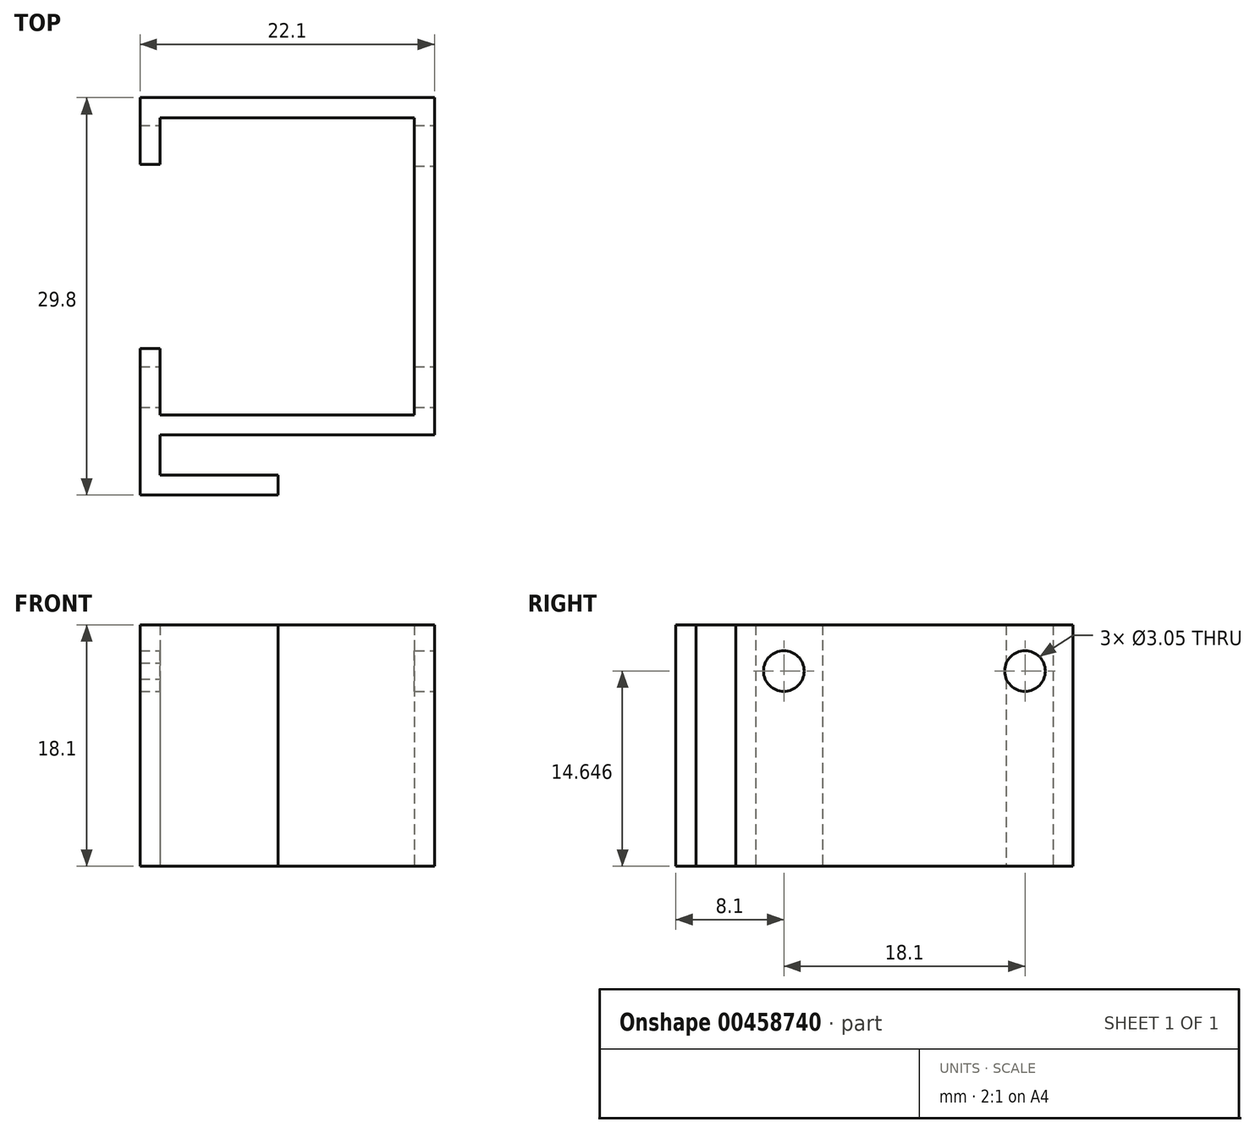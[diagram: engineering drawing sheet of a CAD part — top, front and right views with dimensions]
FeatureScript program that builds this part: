
annotation { "Feature Type Name" : "Feature", "Feature Type Description" : "" }
export const myFeature = defineFeature(function(context is Context, id is Id, definition is map)
    precondition{}
    {
        {
            var Q0;
            Q0=qCreatedBy(makeId("Top.planeOp"),FACE);
            var sketch = newSketch(context, id + "F0", { "sketchPlane" : qUnion([Q0])});
            skLineSegment(sketch, "E0.bottom", {"start": v(-22.1, 18.8) * mm, "end": v(-20.6, 18.8) * mm});
            skLineSegment(sketch, "E0.top", {"start": v(-22.1, 13.8) * mm, "end": v(-20.6, 13.8) * mm});
            skLineSegment(sketch, "E0.left", {"start": v(-22.1, 18.8) * mm, "end": v(-22.1, 13.8) * mm});
            skLineSegment(sketch, "E0.right", {"start": v(-20.6, 18.8) * mm, "end": v(-20.6, 13.8) * mm});
            skPoint(sketch, "E1.oppositeSnap0", {"position": v(-22.1, 17.3) * mm});
            skLineSegment(sketch, "E1.bottom", {"start": v(-22.1, 18.8) * mm, "end": v(0, 18.8) * mm});
            skLineSegment(sketch, "E1.top", {"start": v(-22.1, 17.3) * mm, "end": v(0, 17.3) * mm});
            skLineSegment(sketch, "E1.left", {"start": v(-22.1, 18.8) * mm, "end": v(-22.1, 17.3) * mm});
            skLineSegment(sketch, "E1.right", {"start": v(0, 18.8) * mm, "end": v(0, 17.3) * mm});
            skLineSegment(sketch, "E2.bottom", {"start": v(0, 18.8) * mm, "end": v(-1.5, 18.8) * mm});
            skLineSegment(sketch, "E2.top", {"start": v(0, -6.5) * mm, "end": v(-1.5, -6.5) * mm});
            skLineSegment(sketch, "E2.left", {"start": v(0, 18.8) * mm, "end": v(0, -6.5) * mm});
            skLineSegment(sketch, "E2.right", {"start": v(-1.5, 18.8) * mm, "end": v(-1.5, -6.5) * mm});
            skLineSegment(sketch, "E3.bottom", {"start": v(0, -6.5) * mm, "end": v(-22.1, -6.5) * mm});
            skLineSegment(sketch, "E3.top", {"start": v(0, -5) * mm, "end": v(-22.1, -5) * mm});
            skLineSegment(sketch, "E3.left", {"start": v(0, -6.5) * mm, "end": v(0, -5) * mm});
            skLineSegment(sketch, "E3.right", {"start": v(-22.1, -6.5) * mm, "end": v(-22.1, -5) * mm});
            skLineSegment(sketch, "E4.bottom", {"start": v(-22.1, -6.5) * mm, "end": v(-20.6, -6.5) * mm});
            skLineSegment(sketch, "E4.top", {"start": v(-22.1, 0) * mm, "end": v(-20.6, 0) * mm});
            skLineSegment(sketch, "E4.left", {"start": v(-22.1, -6.5) * mm, "end": v(-22.1, 0) * mm});
            skLineSegment(sketch, "E4.right", {"start": v(-20.6, -6.5) * mm, "end": v(-20.6, 0) * mm});
            skLineSegment(sketch, "E5.top", {"start": v(-22.1, -11) * mm, "end": v(-20.6, -11) * mm});
            skLineSegment(sketch, "E5.left", {"start": v(-22.1, -6.5) * mm, "end": v(-22.1, -11) * mm});
            skLineSegment(sketch, "E5.right", {"start": v(-20.6, -6.5) * mm, "end": v(-20.6, -11) * mm});
            skPoint(sketch, "E6.oppositeSnap0", {"position": v(-20.6, -9.5) * mm});
            skLineSegment(sketch, "E6.bottom", {"start": v(-22.1, -11) * mm, "end": v(-11.74, -11) * mm});
            skLineSegment(sketch, "E6.top", {"start": v(-22.1, -9.5) * mm, "end": v(-11.74, -9.5) * mm});
            skLineSegment(sketch, "E6.left", {"start": v(-22.1, -11) * mm, "end": v(-22.1, -9.5) * mm});
            skLineSegment(sketch, "E6.right", {"start": v(-11.74, -11) * mm, "end": v(-11.74, -9.5) * mm});
            skSolve(sketch);
        }
        {
            var Q0;
            Q0 = qSketchRegion(id + "F0", true);
            extrude(context, id + "F1", {"entities" : qUnion([Q0]), "depth" : 18.1 * mm, "offsetDistance" : 25 * mm});
        }
        {
            var Q0;
            Q0=makeQuery(id+"F1.opExtrude","SWEPT_FACE",FACE,{"disambiguationData":[OSD([sQuery(id+"F0.wireOp",EDGE,"E2.left"),sQuery(id+"F0.wireOp",EDGE,"E3.left")])]});
            var sketch = newSketch(context, id + "F2", { "sketchPlane" : qUnion([Q0])});
            skPoint(sketch, "E7.middle", {"position": v(6.15, 9.05) * mm});
            skLineSegment(sketch, "E8.bottom", {"start": v(17.33, 0) * mm, "end": v(17.32, 18.1) * mm});
            skLineSegment(sketch, "E9.bottom", {"start": v(-5.02, 0) * mm, "end": v(-5.03, 18.1) * mm});
            skCircle(sketch, "E10", {"center": v(-2.9, 14.65) * mm, "radius": 1.52 * mm});
            skLineSegment(sketch, "E11", {"start": v(6.15, -6.58) * mm, "end": v(6.15, 25.63) * mm, "construction": true});
            skCircle(sketch, "E12.MirrorC", {"center": v(15.2, 14.65) * mm, "radius": 1.52 * mm});
            skLineSegment(sketch, "E13", {"start": v(18.8, 9.05) * mm, "end": v(-6.5, 9.05) * mm, "construction": true});
            skSolve(sketch);
        }
        {
            var Q0;
            Q0 = qSketchRegion(id + "F2", true);
            extrude(context, id + "F3", {"entities" : qUnion([Q0]), "operationType" : NewBodyOperationType.REMOVE, "oppositeDirection" : true, "depth" : 25 * mm, "offsetDistance" : 25 * mm});
        }
    });
